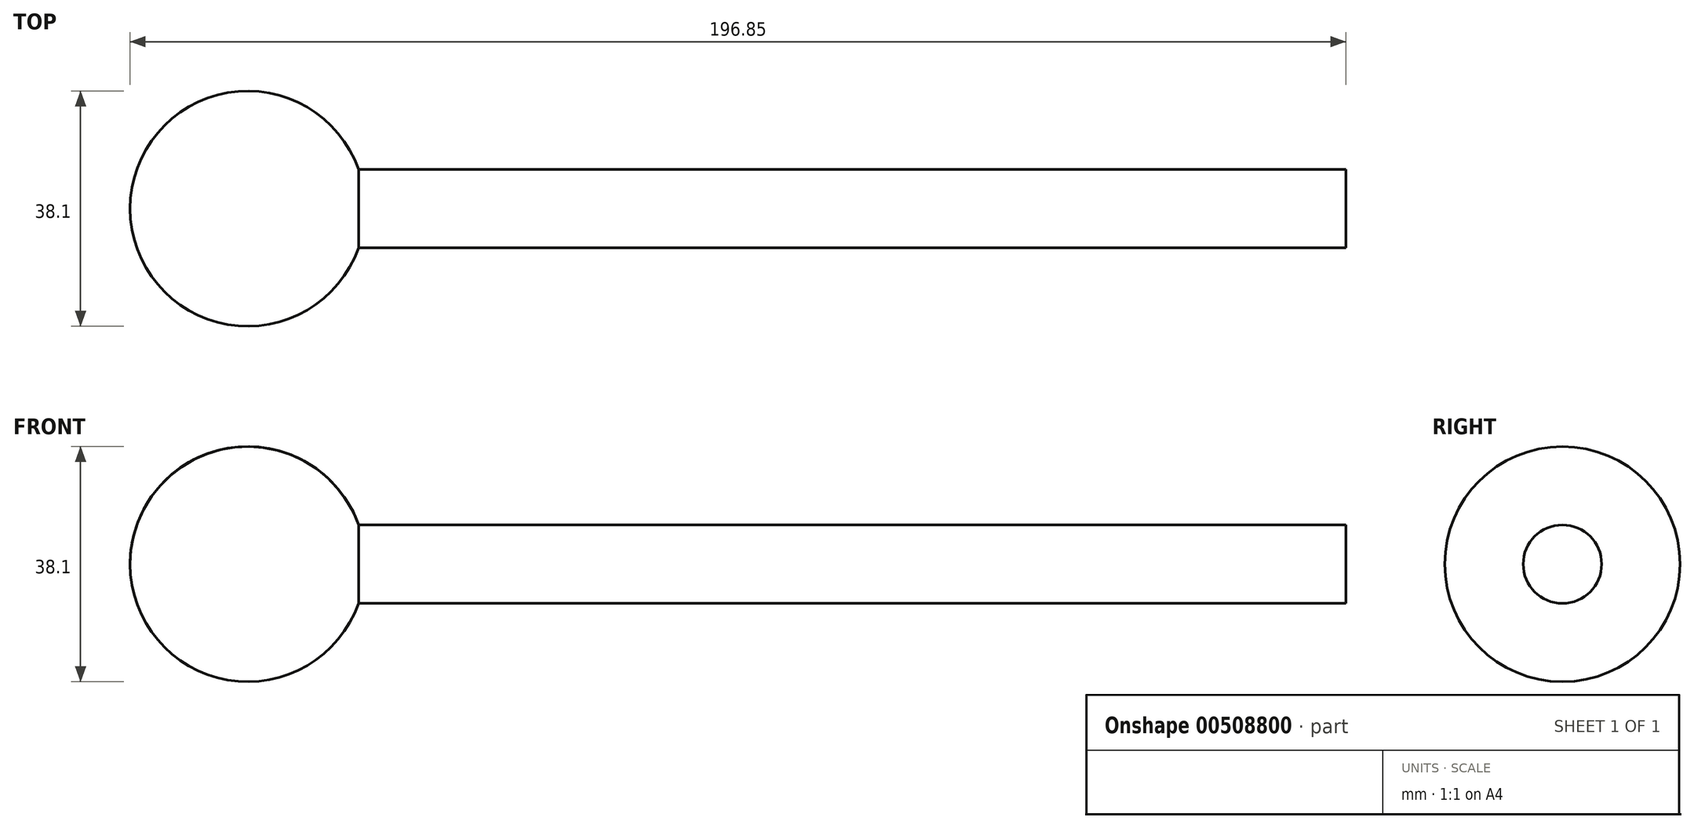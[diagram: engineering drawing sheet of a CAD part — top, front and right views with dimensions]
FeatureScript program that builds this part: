
annotation { "Feature Type Name" : "Feature", "Feature Type Description" : "" }
export const myFeature = defineFeature(function(context is Context, id is Id, definition is map)
    precondition{}
    {
        {
            var Q0;
            Q0=qCreatedBy(makeId("Front.planeOp"),FACE);
            var sketch = newSketch(context, id + "F0", { "sketchPlane" : qUnion([Q0])});
            skLineSegment(sketch, "E0", {"start": v(0, 0) * mm, "end": v(0, 6.35) * mm});
            skLineSegment(sketch, "E1", {"start": v(0, 6.35) * mm, "end": v(-158.75, 6.35) * mm});
            skLineSegment(sketch, "E2", {"start": v(0, 0) * mm, "end": v(-196.85, 0) * mm});
            skArc(sketch, "E3", {"start": v(-159.84, 6.35) * mm, "mid": v(-181.02, 18.78) * mm, "end": v(-196.85, 0) * mm});
            skLineSegment(sketch, "E4", {"start": v(-158.75, 6.35) * mm, "end": v(-159.84, 6.35) * mm});
            skSolve(sketch);
        }
        {
            var Q0;
            Q0=makeQuery(id+"F0.imprint","IMPRINT",FACE,{"disambiguationData":[TD([[makeQuery(id+"F0.imprint","IMPRINT",EDGE,{"derivedFrom":sQuery(id+"F0.wireOp",EDGE,"E0")}),1.0]])]});
            var Q1;
            Q1=sQuery(id+"F0.wireOp",EDGE,"E2");
            revolve(context, id + "F1", {"entities" : qUnion([Q0]), "axis" : qUnion([Q1]), "revolveType" : RevolveType.FULL});
        }
    });
